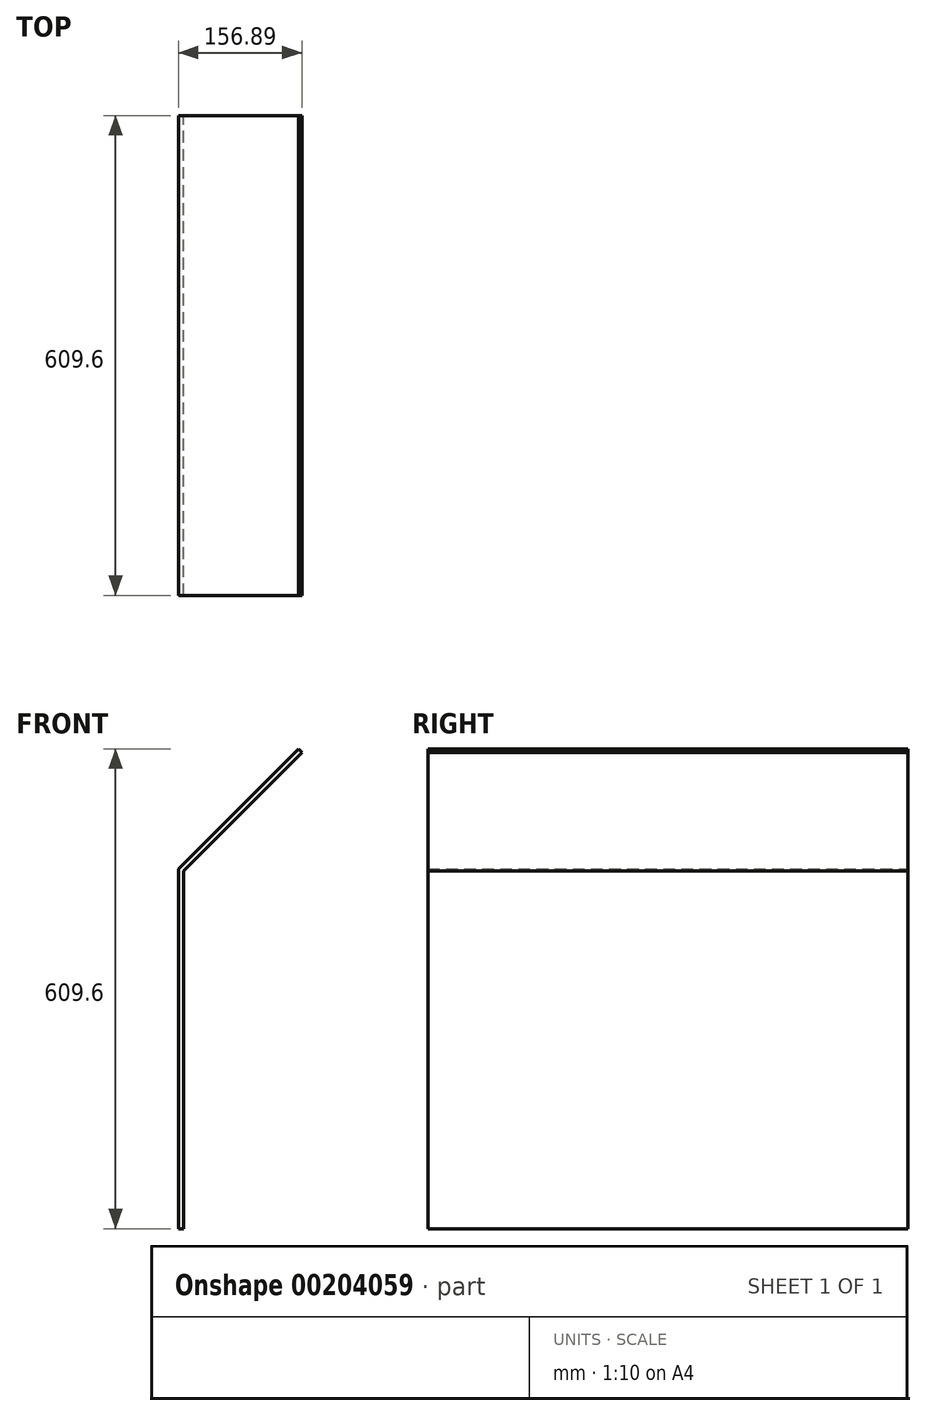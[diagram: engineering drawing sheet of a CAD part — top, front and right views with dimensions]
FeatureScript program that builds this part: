
annotation { "Feature Type Name" : "Feature", "Feature Type Description" : "" }
export const myFeature = defineFeature(function(context is Context, id is Id, definition is map)
    precondition{}
    {
        {
            var Q0;
            Q0=qCreatedBy(makeId("Front.planeOp"),FACE);
            var sketch = newSketch(context, id + "F0", { "sketchPlane" : qUnion([Q0])});
            skLineSegment(sketch, "E0", {"start": v(0, 0) * mm, "end": v(0, 457.2) * mm});
            skLineSegment(sketch, "E1", {"start": v(152.4, 609.6) * mm, "end": v(0, 457.2) * mm});
            skPoint(sketch, "E2.start.orphan", {"position": v(0, 609.6) * mm});
            skLineSegment(sketch, "E3.0", {"start": v(156.9, 605.1) * mm, "end": v(6.35, 454.57) * mm});
            skLineSegment(sketch, "E3.1", {"start": v(6.35, 0) * mm, "end": v(6.35, 454.57) * mm});
            skLineSegment(sketch, "E4", {"start": v(152.4, 609.6) * mm, "end": v(156.9, 605.1) * mm});
            skLineSegment(sketch, "E5", {"start": v(0, 0) * mm, "end": v(6.35, 0) * mm});
            skSolve(sketch);
        }
        {
            var Q0;
            Q0 = qSketchRegion(id + "F0", true);
            extrude(context, id + "F1", {"entities" : qUnion([Q0]), "endBound" : BoundingType.SYMMETRIC, "depth" : 609.6 * mm});
        }
    });
